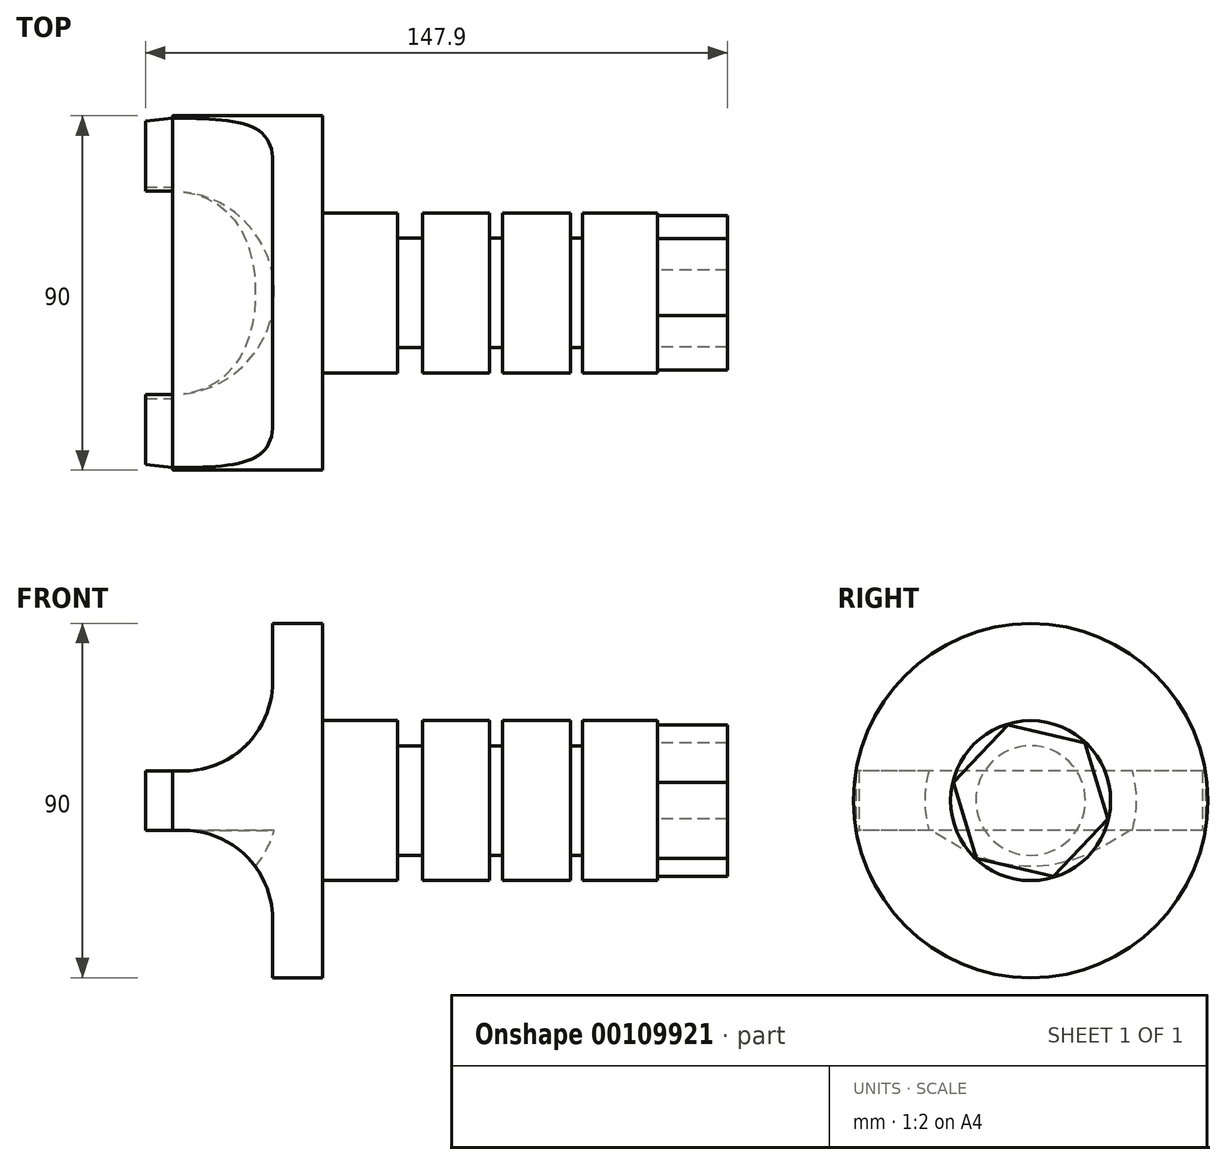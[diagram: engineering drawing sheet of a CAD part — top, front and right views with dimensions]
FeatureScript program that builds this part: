
annotation { "Feature Type Name" : "Feature", "Feature Type Description" : "" }
export const myFeature = defineFeature(function(context is Context, id is Id, definition is map)
    precondition{}
    {
        {
            var Q0;
            Q0=qCreatedBy(makeId("Right.planeOp"),FACE);
            var sketch = newSketch(context, id + "F0", { "sketchPlane" : qUnion([Q0])});
            skCircle(sketch, "E0", {"center": v(0, 0) * mm, "radius": 45 * mm});
            skSolve(sketch);
        }
        {
            var Q0;
            Q0 = qSketchRegion(id + "F0", true);
            extrude(context, id + "F1", {"entities" : qUnion([Q0]), "oppositeDirection" : true, "depth" : 38.1 * mm});
        }
        {
            var Q0;
            Q0=makeQuery(id+"F1.opExtrude","CAP_FACE",FACE,{"disambiguationData":[OSD([sQuery(id+"F0.wireOp",EDGE,"E0")])],"isStart":true});
            var sketch = newSketch(context, id + "F2", { "sketchPlane" : qUnion([Q0])});
            skCircle(sketch, "E1", {"center": v(0, 0) * mm, "radius": 13.9 * mm});
            skSolve(sketch);
        }
        {
            var Q0;
            Q0 = qSketchRegion(id + "F2", true);
            extrude(context, id + "F3", {"entities" : qUnion([Q0]), "operationType" : NewBodyOperationType.ADD, "depth" : 92.4 * mm});
        }
        {
            var Q0;
            Q0=qCreatedBy(makeId("Right.planeOp"),FACE);
            cPlane(context, id + "F4", {"entities" : qUnion([Q0]), "cplaneType" : CPlaneType.OFFSET, "offset" : 25.4 * mm, "width" : 152.4 * mm, "height" : 152.4 * mm});
        }
        {
            var Q0;
            Q0=qCreatedBy(id+"F4.planeOp",FACE);
            cPlane(context, id + "F5", {"entities" : qUnion([Q0]), "cplaneType" : CPlaneType.OFFSET, "offset" : 20.32 * mm, "width" : 152.4 * mm, "height" : 152.4 * mm});
        }
        {
            var Q0;
            Q0=qCreatedBy(id+"F5.planeOp",FACE);
            cPlane(context, id + "F6", {"entities" : qUnion([Q0]), "cplaneType" : CPlaneType.OFFSET, "offset" : 20.32 * mm, "width" : 152.4 * mm, "height" : 152.4 * mm});
        }
        {
            var Q0;
            Q0=qCreatedBy(makeId("Right.planeOp"),FACE);
            var sketch = newSketch(context, id + "F7", { "sketchPlane" : qUnion([Q0])});
            skCircle(sketch, "E2", {"center": v(0, 0) * mm, "radius": 20.32 * mm});
            skSolve(sketch);
        }
        {
            var Q0;
            Q0 = qSketchRegion(id + "F7", true);
            extrude(context, id + "F8", {"entities" : qUnion([Q0]), "operationType" : NewBodyOperationType.ADD, "depth" : 19.05 * mm});
        }
        {
            var Q0;
            Q0=qCreatedBy(id+"F4.planeOp",FACE);
            var sketch = newSketch(context, id + "F9", { "sketchPlane" : qUnion([Q0])});
            skCircle(sketch, "E3", {"center": v(0, 0) * mm, "radius": 20.32 * mm});
            skSolve(sketch);
        }
        {
            var Q0;
            Q0 = qSketchRegion(id + "F9", true);
            extrude(context, id + "F10", {"entities" : qUnion([Q0]), "operationType" : NewBodyOperationType.ADD, "depth" : 16.96 * mm});
        }
        {
            var Q0;
            Q0=qCreatedBy(id+"F5.planeOp",FACE);
            var sketch = newSketch(context, id + "F11", { "sketchPlane" : qUnion([Q0])});
            skCircle(sketch, "E4", {"center": v(0, 0) * mm, "radius": 20.32 * mm});
            skSolve(sketch);
        }
        {
            var Q0;
            Q0 = qSketchRegion(id + "F11", true);
            extrude(context, id + "F12", {"entities" : qUnion([Q0]), "operationType" : NewBodyOperationType.ADD, "depth" : 17.2 * mm});
        }
        {
            var Q0;
            Q0=qCreatedBy(id+"F6.planeOp",FACE);
            var sketch = newSketch(context, id + "F13", { "sketchPlane" : qUnion([Q0])});
            skCircle(sketch, "E5", {"center": v(0, 0) * mm, "radius": 20.32 * mm});
            skSolve(sketch);
        }
        {
            var Q0;
            Q0 = qSketchRegion(id + "F13", true);
            extrude(context, id + "F14", {"entities" : qUnion([Q0]), "operationType" : NewBodyOperationType.ADD, "depth" : 19.05 * mm});
        }
        {
            var Q0;
            Q0=makeQuery(id+"F14.opExtrude","CAP_FACE",FACE,{"disambiguationData":[OSD([sQuery(id+"F13.wireOp",EDGE,"E5")])],"isStart":false});
            var sketch = newSketch(context, id + "F15", { "sketchPlane" : qUnion([Q0])});
            skCircle(sketch, "E6.cCircle", {"center": v(0, 0) * mm, "radius": 17.44 * mm, "construction": true});
            skLineSegment(sketch, "E6.0", {"start": v(-5.8, 19.28) * mm, "end": v(13.8, 14.67) * mm});
            skLineSegment(sketch, "E6.1", {"start": v(13.8, 14.67) * mm, "end": v(19.6, -4.61) * mm});
            skLineSegment(sketch, "E6.2", {"start": v(19.6, -4.61) * mm, "end": v(5.8, -19.28) * mm});
            skLineSegment(sketch, "E6.3", {"start": v(5.8, -19.28) * mm, "end": v(-13.8, -14.67) * mm});
            skLineSegment(sketch, "E6.4", {"start": v(-13.8, -14.67) * mm, "end": v(-19.6, 4.61) * mm});
            skLineSegment(sketch, "E6.5", {"start": v(-19.6, 4.61) * mm, "end": v(-5.8, 19.28) * mm});
            skPoint(sketch, "E6.0.midPoint", {"position": v(4, 16.97) * mm});
            skSolve(sketch);
        }
        {
            var Q0;
            Q0 = qSketchRegion(id + "F15", true);
            extrude(context, id + "F16", {"entities" : qUnion([Q0]), "operationType" : NewBodyOperationType.ADD, "depth" : 17.78 * mm});
        }
        {
            var Q0;
            Q0=makeQuery(id+"F1.opExtrude","CAP_FACE",FACE,{"disambiguationData":[OSD([sQuery(id+"F0.wireOp",EDGE,"E0")])],"isStart":false});
            var sketch = newSketch(context, id + "F17", { "sketchPlane" : qUnion([Q0])});
            skLineSegment(sketch, "E7.bottom", {"start": v(-44.36, 7.54) * mm, "end": v(44.5, 7.54) * mm});
            skLineSegment(sketch, "E7.top", {"start": v(-44.36, 46.92) * mm, "end": v(44.5, 46.92) * mm});
            skLineSegment(sketch, "E7.left", {"start": v(-44.36, 7.54) * mm, "end": v(-44.36, 46.92) * mm});
            skLineSegment(sketch, "E7.right", {"start": v(44.5, 7.54) * mm, "end": v(44.5, 46.92) * mm});
            skLineSegment(sketch, "E8.MirrorCS", {"start": v(-44.36, -7.54) * mm, "end": v(44.5, -7.54) * mm});
            skLineSegment(sketch, "E9.MirrorCS", {"start": v(-44.36, -7.54) * mm, "end": v(-44.36, -46.92) * mm});
            skLineSegment(sketch, "E10.MirrorCS", {"start": v(-44.36, -46.92) * mm, "end": v(44.5, -46.92) * mm});
            skLineSegment(sketch, "E11.MirrorCS", {"start": v(44.5, -7.54) * mm, "end": v(44.5, -46.92) * mm});
            skSolve(sketch);
        }
        {
            var Q0;
            Q0 = qSketchRegion(id + "F17", true);
            extrude(context, id + "F18", {"entities" : qUnion([Q0]), "operationType" : NewBodyOperationType.REMOVE, "oppositeDirection" : true, "depth" : 25.4 * mm});
        }
        {
            var Q0;
            Q0=makeQuery(id+"F18.boolean.opBoolean","COPY",EDGE,{"derivedFrom":makeQuery(id+"F18.opExtrude","CAP_EDGE",EDGE,{"disambiguationData":[OSD([sQuery(id+"F17.wireOp",EDGE,"E7.bottom")])],"isStart":false})});
            var Q1;
            Q1=makeQuery(id+"F18.boolean.opBoolean","COPY",EDGE,{"derivedFrom":makeQuery(id+"F18.opExtrude","CAP_EDGE",EDGE,{"disambiguationData":[OSD([sQuery(id+"F17.wireOp",EDGE,"E8.MirrorCS")])],"isStart":false})});
            fillet(context, id + "F19", {"entities" : qUnion([Q0, Q1]), "radius" : 22.63 * mm, "tangentPropagation" : true, "allowEdgeOverflow" : false});
        }
        {
            var Q0;
            Q0=makeQuery(id+"F1.opExtrude","CAP_FACE",FACE,{"disambiguationData":[OSD([sQuery(id+"F0.wireOp",EDGE,"E0")])],"isStart":false});
            var sketch = newSketch(context, id + "F20", { "sketchPlane" : qUnion([Q0])});
            skLineSegment(sketch, "E12", {"start": v(0, 0) * mm, "end": v(0, 53.78) * mm});
            skLineSegment(sketch, "E13", {"start": v(0, 53.78) * mm, "end": v(0, -32.95) * mm});
            skPoint(sketch, "E13.endSnap0", {"position": v(0, -7.54) * mm});
            skArc(sketch, "E14", {"start": v(0, 26.9) * mm, "mid": v(-26.9, 0) * mm, "end": v(0, -26.9) * mm});
            skSolve(sketch);
        }
        {
            var Q0;
            {var subQ0=sQuery(id+"F20.wireOp",EDGE,"E14");var subQ1=sQuery(id+"F20.wireOp",EDGE,"E13");var subQ2=makeQuery(id+"F20.imprint","INTERSECT",VERTEX,{"disambiguationData":[OD(0.0)],"derivedFrom":[subQ1,subQ0]});Q0=makeQuery(id+"F20.imprint","IMPRINT",FACE,{"disambiguationData":[TD([[makeQuery(id+"F20.imprint","IMPRINT",EDGE,{"disambiguationData":[TD([[subQ2,-1.0]])],"derivedFrom":subQ1}),-1.0]])]});}
            var Q1;
            {var subQ0=sQuery(id+"F20.wireOp",EDGE,"E13");var subQ5=makeQuery(id+"F20.imprint","IMPRINT",VERTEX,{"derivedFrom":subQ0});Q1=makeQuery(id+"F20.imprint","IMPRINT",FACE,{"disambiguationData":[TD([[makeQuery(id+"F20.imprint","IMPRINT",EDGE,{"disambiguationData":[TD([[subQ5,1.0]])],"derivedFrom":subQ0}),-1.0]])]});}
            var Q2;
            {var subQ0=sQuery(id+"F20.wireOp",EDGE,"E14");var subQ1=sQuery(id+"F20.wireOp",EDGE,"E13");var subQ2=makeQuery(id+"F20.imprint","INTERSECT",VERTEX,{"disambiguationData":[OD(1.0)],"derivedFrom":[subQ1,subQ0]});Q2=makeQuery(id+"F20.imprint","IMPRINT",FACE,{"disambiguationData":[TD([[makeQuery(id+"F20.imprint","IMPRINT",EDGE,{"disambiguationData":[TD([[subQ2,1.0]])],"derivedFrom":subQ1}),-1.0]])]});}
            var Q3;
            Q3=sQuery(id+"F20.wireOp",EDGE,"E13");
            revolve(context, id + "F21", {"operationType" : NewBodyOperationType.REMOVE, "entities" : qUnion([Q0, Q1, Q2]), "axis" : qUnion([Q3]), "revolveType" : RevolveType.FULL, "oppositeDirection" : true});
        }
        {
            var Q0;
            Q0=makeQuery(id+"F21.boolean.opBoolean","SPLIT",FACE,{"disambiguationData":[OD(0.0)],"derivedFrom":makeQuery(id+"F1.opExtrude","CAP_FACE",FACE,{"disambiguationData":[OSD([sQuery(id+"F0.wireOp",EDGE,"E0")])],"isStart":false})});
            var sketch = newSketch(context, id + "F22", { "sketchPlane" : qUnion([Q0])});
            skLineSegment(sketch, "E15.0", {"start": v(-44.36, 7.54) * mm, "end": v(-25.81, 7.54) * mm});
            skArc(sketch, "E16.0", {"start": v(-44.36, -7.54) * mm, "mid": v(-45, 0) * mm, "end": v(-44.36, 7.54) * mm});
            skLineSegment(sketch, "E17.0", {"start": v(-44.36, -7.54) * mm, "end": v(-25.81, -7.54) * mm});
            skArc(sketch, "E18.0", {"start": v(-25.81, 7.54) * mm, "mid": v(-26.9, 0) * mm, "end": v(-25.81, -7.54) * mm});
            skArc(sketch, "E19.0", {"start": v(25.81, -7.54) * mm, "mid": v(26.9, 0) * mm, "end": v(25.81, 7.54) * mm});
            skLineSegment(sketch, "E20.0", {"start": v(25.81, 7.54) * mm, "end": v(44.36, 7.54) * mm});
            skArc(sketch, "E21.0", {"start": v(44.36, 7.54) * mm, "mid": v(45, 0) * mm, "end": v(44.36, -7.54) * mm});
            skLineSegment(sketch, "E22.0", {"start": v(25.81, -7.54) * mm, "end": v(44.36, -7.54) * mm});
            skSolve(sketch);
        }
        {
            var Q0;
            Q0 = qSketchRegion(id + "F22", true);
            extrude(context, id + "F23", {"entities" : qUnion([Q0]), "depth" : 6.93 * mm});
        }
        {
            var Q0;
            Q0=makeQuery(id+"F23.opExtrude","SWEPT_FACE",FACE,{"disambiguationData":[OSD([sQuery(id+"F22.wireOp",EDGE,"E22.0")])]});
            var sketch = newSketch(context, id + "F24", { "sketchPlane" : qUnion([Q0])});
            skLineSegment(sketch, "E23", {"start": v(-38.1, 44.36) * mm, "end": v(-45.03, 43.63) * mm});
            skLineSegment(sketch, "E24", {"start": v(-45.03, 43.63) * mm, "end": v(-45.03, 44.36) * mm});
            skLineSegment(sketch, "E25.MirrorCS", {"start": v(-38.1, -44.36) * mm, "end": v(-45.03, -43.63) * mm});
            skLineSegment(sketch, "E26.MirrorCS", {"start": v(-45.03, -44.36) * mm, "end": v(-38.1, -44.36) * mm});
            skLineSegment(sketch, "E27", {"start": v(-45.03, -43.63) * mm, "end": v(-45.03, -44.36) * mm});
            skLineSegment(sketch, "E28", {"start": v(-45.03, 43.63) * mm, "end": v(-45.03, 47.23) * mm});
            skLineSegment(sketch, "E29", {"start": v(-45.03, 47.23) * mm, "end": v(-38.1, 47.23) * mm});
            skLineSegment(sketch, "E30", {"start": v(-38.1, 47.23) * mm, "end": v(-38.1, 44.36) * mm});
            skLineSegment(sketch, "E31.MirrorCS", {"start": v(-45.03, -47.23) * mm, "end": v(-38.1, -47.23) * mm});
            skLineSegment(sketch, "E32.MirrorCS", {"start": v(-45.03, -43.63) * mm, "end": v(-45.03, -47.23) * mm});
            skLineSegment(sketch, "E33.MirrorCS", {"start": v(-38.1, -47.23) * mm, "end": v(-38.1, -44.36) * mm});
            skSolve(sketch);
        }
        {
            var Q0;
            Q0 = qSketchRegion(id + "F24", true);
            extrude(context, id + "F25", {"entities" : qUnion([Q0]), "operationType" : NewBodyOperationType.REMOVE, "oppositeDirection" : true, "depth" : 25.4 * mm});
        }
    });
